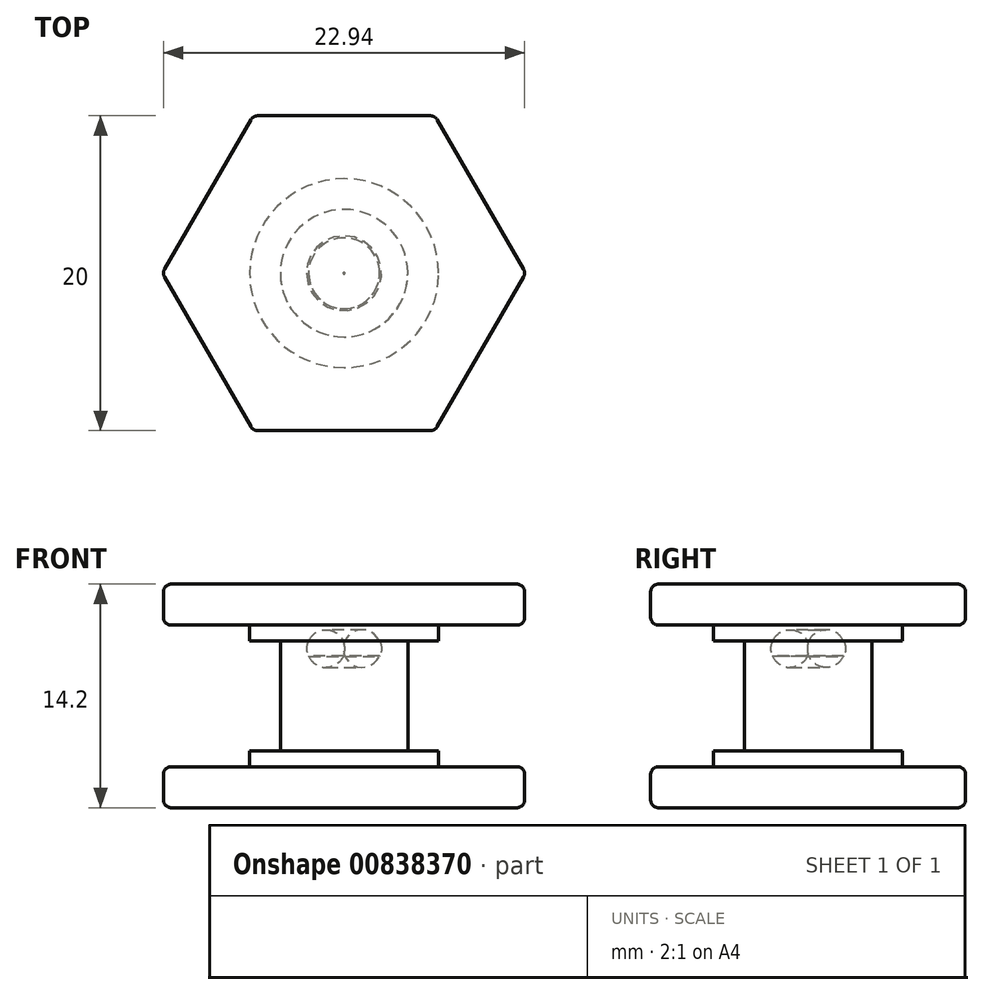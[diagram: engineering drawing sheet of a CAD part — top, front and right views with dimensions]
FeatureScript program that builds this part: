
annotation { "Feature Type Name" : "Feature", "Feature Type Description" : "" }
export const myFeature = defineFeature(function(context is Context, id is Id, definition is map)
    precondition{}
    {
        {
            var Q0;
            Q0=qCreatedBy(makeId("Top.planeOp"),FACE);
            var sketch = newSketch(context, id + "F0", { "sketchPlane" : qUnion([Q0])});
            skCircle(sketch, "E0", {"center": v(0, 0) * mm, "radius": 4.05 * mm});
            skCircle(sketch, "E1", {"center": v(0, 0) * mm, "radius": 6 * mm});
            skSolve(sketch);
        }
        {
            var Q0;
            Q0 = qSketchRegion(id + "F0", true);
            var Q1;
            Q1=makeQuery(id+"F0.imprint","IMPRINT",FACE,{"disambiguationData":[TD([[makeQuery(id+"F0.imprint","IMPRINT",EDGE,{"derivedFrom":sQuery(id+"F0.wireOp",EDGE,"E0")}),1.0]])]});
            extrude(context, id + "F1", {"entities" : qUnion([Q0, Q1]), "depth" : 1 * mm, "offsetDistance" : 25 * mm});
        }
        {
            var Q0;
            Q0=makeQuery(id+"F0.imprint","IMPRINT",FACE,{"disambiguationData":[TD([[makeQuery(id+"F0.imprint","IMPRINT",EDGE,{"derivedFrom":sQuery(id+"F0.wireOp",EDGE,"E0")}),1.0]])]});
            extrude(context, id + "F2", {"entities" : qUnion([Q0]), "operationType" : NewBodyOperationType.ADD, "oppositeDirection" : true, "depth" : 7 * mm, "offsetDistance" : 25 * mm});
        }
        {
            var Q0;
            Q0=makeQuery(id+"F1.opExtrude","CAP_FACE",FACE,{"disambiguationData":[OSD([sQuery(id+"F0.wireOp",EDGE,"E1")])],"isStart":false});
            var sketch = newSketch(context, id + "F3", { "sketchPlane" : qUnion([Q0])});
            skCircle(sketch, "E2.cCircle", {"center": v(0, 0) * mm, "radius": 10 * mm, "construction": true});
            skLineSegment(sketch, "E2.0", {"start": v(5.77, -10) * mm, "end": v(-5.77, -10) * mm});
            skLineSegment(sketch, "E2.1", {"start": v(-5.77, -10) * mm, "end": v(-11.55, 0) * mm});
            skLineSegment(sketch, "E2.2", {"start": v(-11.55, 0) * mm, "end": v(-5.77, 10) * mm});
            skLineSegment(sketch, "E2.3", {"start": v(-5.77, 10) * mm, "end": v(5.77, 10) * mm});
            skLineSegment(sketch, "E2.4", {"start": v(5.77, 10) * mm, "end": v(11.55, 0) * mm});
            skLineSegment(sketch, "E2.5", {"start": v(11.55, 0) * mm, "end": v(5.77, -10) * mm});
            skPoint(sketch, "E2.0.midPoint", {"position": v(0, -10) * mm});
            skSolve(sketch);
        }
        {
            var Q0;
            Q0 = qSketchRegion(id + "F3", true);
            extrude(context, id + "F4", {"entities" : qUnion([Q0]), "operationType" : NewBodyOperationType.ADD, "depth" : 2.6 * mm, "offsetDistance" : 25 * mm});
        }
        {
            var Q0;
            Q0=makeQuery(id+"F2.opExtrude","CAP_FACE",FACE,{"disambiguationData":[OSD([sQuery(id+"F0.wireOp",EDGE,"E0")])],"isStart":false});
            var sketch = newSketch(context, id + "F5", { "sketchPlane" : qUnion([Q0])});
            skCircle(sketch, "E3.0", {"center": v(0, 0) * mm, "radius": 6 * mm});
            skSolve(sketch);
        }
        {
            var Q0;
            Q0=makeQuery(id+"F5.imprint","IMPRINT",FACE,{"disambiguationData":[TD([[makeQuery(id+"F5.imprint","IMPRINT",EDGE,{"derivedFrom":sQuery(id+"F5.wireOp",EDGE,"E3.0")}),1.0]])]});
            var Q1;
            Q1=makeQuery(id+"F5.imprint","IMPRINT",FACE,{"disambiguationData":[TD([[makeQuery(id+"F5.imprint","IMPRINT",EDGE,{"derivedFrom":makeQuery(id+"F2.opExtrude","CAP_EDGE",EDGE,{"disambiguationData":[OSD([sQuery(id+"F0.wireOp",EDGE,"E0")])],"isStart":false})}),-1.0]])]});
            extrude(context, id + "F6", {"entities" : qUnion([Q0, Q1]), "depth" : 1 * mm, "offsetDistance" : 25 * mm});
        }
        {
            var Q0;
            Q0=makeQuery(id+"F6.opExtrude","CAP_FACE",FACE,{"disambiguationData":[OSD([sQuery(id+"F5.wireOp",EDGE,"E3.0")])],"isStart":false});
            var sketch = newSketch(context, id + "F7", { "sketchPlane" : qUnion([Q0])});
            skLineSegment(sketch, "E4.0", {"start": v(11.55, 0) * mm, "end": v(5.77, 10) * mm});
            skLineSegment(sketch, "E4.1", {"start": v(5.77, 10) * mm, "end": v(-5.77, 10) * mm});
            skLineSegment(sketch, "E4.2", {"start": v(-5.77, 10) * mm, "end": v(-11.55, 0) * mm});
            skLineSegment(sketch, "E4.3", {"start": v(-11.55, 0) * mm, "end": v(-5.77, -10) * mm});
            skLineSegment(sketch, "E4.4", {"start": v(-5.77, -10) * mm, "end": v(5.77, -10) * mm});
            skLineSegment(sketch, "E4.5", {"start": v(5.77, -10) * mm, "end": v(11.55, 0) * mm});
            skSolve(sketch);
        }
        {
            var Q0;
            Q0 = qSketchRegion(id + "F7", true);
            extrude(context, id + "F8", {"entities" : qUnion([Q0]), "operationType" : NewBodyOperationType.ADD, "depth" : 2.6 * mm, "offsetDistance" : 25 * mm});
        }
        {
            var Q0;
            Q0=makeQuery(id+"F4.opExtrude","SWEPT_FACE",FACE,{"disambiguationData":[OSD([sQuery(id+"F3.wireOp",EDGE,"E2.5")])]});
            var Q1;
            Q1=makeQuery(id+"F4.opExtrude","SWEPT_FACE",FACE,{"disambiguationData":[OSD([sQuery(id+"F3.wireOp",EDGE,"E2.4")])]});
            var Q2;
            Q2=makeQuery(id+"F4.opExtrude","SWEPT_FACE",FACE,{"disambiguationData":[OSD([sQuery(id+"F3.wireOp",EDGE,"E2.0")])]});
            var Q3;
            Q3=makeQuery(id+"F4.opExtrude","SWEPT_FACE",FACE,{"disambiguationData":[OSD([sQuery(id+"F3.wireOp",EDGE,"E2.1")])]});
            var Q4;
            Q4=makeQuery(id+"F4.opExtrude","SWEPT_FACE",FACE,{"disambiguationData":[OSD([sQuery(id+"F3.wireOp",EDGE,"E2.2")])]});
            var Q5;
            Q5=makeQuery(id+"F4.opExtrude","SWEPT_FACE",FACE,{"disambiguationData":[OSD([sQuery(id+"F3.wireOp",EDGE,"E2.3")])]});
            var Q6;
            Q6=makeQuery(id+"F8.opExtrude","SWEPT_FACE",FACE,{"disambiguationData":[OSD([sQuery(id+"F7.wireOp",EDGE,"E4.1")])]});
            var Q7;
            Q7=makeQuery(id+"F8.opExtrude","SWEPT_FACE",FACE,{"disambiguationData":[OSD([sQuery(id+"F7.wireOp",EDGE,"E4.0")])]});
            var Q8;
            Q8=makeQuery(id+"F8.opExtrude","SWEPT_FACE",FACE,{"disambiguationData":[OSD([sQuery(id+"F7.wireOp",EDGE,"E4.5")])]});
            var Q9;
            Q9=makeQuery(id+"F8.opExtrude","SWEPT_FACE",FACE,{"disambiguationData":[OSD([sQuery(id+"F7.wireOp",EDGE,"E4.4")])]});
            var Q10;
            Q10=makeQuery(id+"F8.opExtrude","SWEPT_FACE",FACE,{"disambiguationData":[OSD([sQuery(id+"F7.wireOp",EDGE,"E4.3")])]});
            var Q11;
            Q11=makeQuery(id+"F8.opExtrude","SWEPT_FACE",FACE,{"disambiguationData":[OSD([sQuery(id+"F7.wireOp",EDGE,"E4.2")])]});
            fillet(context, id + "F9", {"entities" : qUnion([Q0, Q1, Q2, Q3, Q4, Q5, Q6, Q7, Q8, Q9, Q10, Q11]), "radius" : .5 * mm, "tangentPropagation" : true, "allowEdgeOverflow" : false});
        }
        {
            var Q0;
            Q0=makeQuery(id+"F2.opExtrude","CAP_FACE",FACE,{"disambiguationData":[OSD([sQuery(id+"F0.wireOp",EDGE,"E0")])],"isStart":false});
            var sketch = newSketch(context, id + "F10", { "sketchPlane" : qUnion([Q0])});
            skCircle(sketch, "E5", {"center": v(0, 0) * mm, "radius": 2.25 * mm});
            skSolve(sketch);
        }
        {
            var Q0;
            Q0=makeQuery(id+"F10.imprint","IMPRINT",FACE,{"disambiguationData":[TD([[makeQuery(id+"F10.imprint","IMPRINT",EDGE,{"derivedFrom":sQuery(id+"F10.wireOp",EDGE,"E5")}),1.0]])]});
            extrude(context, id + "F11", {"entities" : qUnion([Q0]), "operationType" : NewBodyOperationType.REMOVE, "oppositeDirection" : true, "depth" : 7 * mm, "offsetDistance" : 25 * mm});
        }
        {
            var Q0;
            Q0=qCreatedBy(makeId("Right.planeOp"),FACE);
            var sketch = newSketch(context, id + "F12", { "sketchPlane" : qUnion([Q0])});
            skArc(sketch, "E6", {"start": v(2.25, -1) * mm, "mid": v(2.38, -0.5) * mm, "end": v(2.25, 0) * mm});
            skLineSegment(sketch, "E7", {"start": v(0, 0) * mm, "end": v(0, -7.74) * mm, "construction": true});
            skLineSegment(sketch, "E8", {"start": v(2.25, 0) * mm, "end": v(2.25, -1) * mm});
            skSolve(sketch);
        }
        {
            var Q0;
            Q0 = qSketchRegion(id + "F12", true);
            var Q1;
            Q1=sQuery(id+"F12.wireOp",EDGE,"E7");
            revolve(context, id + "F13", {"operationType" : NewBodyOperationType.REMOVE, "surfaceOperationType" : NewSurfaceOperationType.NEW, "entities" : qUnion([Q0]), "axis" : qUnion([Q1]), "revolveType" : RevolveType.FULL, "oppositeDirection" : true});
        }
        {
            var Q0;
            Q0=makeQuery(id+"F6.opExtrude","CAP_FACE",FACE,{"disambiguationData":[OSD([sQuery(id+"F5.wireOp",EDGE,"E3.0")])],"isStart":true});
            var sketch = newSketch(context, id + "F14", { "sketchPlane" : qUnion([Q0])});
            skCircle(sketch, "E9.0", {"center": v(0, 0) * mm, "radius": 2.25 * mm});
            skSolve(sketch);
        }
        {
            var Q0;
            Q0 = qSketchRegion(id + "F14", true);
            var Q1;
            Q1=makeQuery(id+"F11.boolean.opBoolean","COPY",FACE,{"derivedFrom":makeQuery(id+"F11.opExtrude","CAP_FACE",FACE,{"disambiguationData":[OSD([sQuery(id+"F10.wireOp",EDGE,"E5")])],"isStart":false})});
            extrude(context, id + "F15", {"entities" : qUnion([Q0]), "operationType" : NewBodyOperationType.ADD, "endBound" : BoundingType.UP_TO_SURFACE, "depth" : 25 * mm, "endBoundEntityFace" : qUnion([Q1]), "offsetDistance" : 25 * mm});
        }
        {
            var Q0;
            Q0=qCreatedBy(makeId("Right.planeOp"),FACE);
            var sketch = newSketch(context, id + "F16", { "sketchPlane" : qUnion([Q0])});
            skLineSegment(sketch, "E10", {"start": v(-2.24, 0) * mm, "end": v(-2.24, -0.98) * mm});
            skArc(sketch, "E11", {"start": v(-2.24, 0) * mm, "mid": v(-2.35, -0.5) * mm, "end": v(-2.24, -0.98) * mm});
            skLineSegment(sketch, "E12", {"start": v(0, 0) * mm, "end": v(0, -7.4) * mm, "construction": true});
            skSolve(sketch);
        }
        {
            var Q0;
            Q0 = qSketchRegion(id + "F16", true);
            var Q1;
            Q1=sQuery(id+"F16.wireOp",EDGE,"E12");
            revolve(context, id + "F17", {"operationType" : NewBodyOperationType.ADD, "surfaceOperationType" : NewSurfaceOperationType.NEW, "entities" : qUnion([Q0]), "axis" : qUnion([Q1]), "revolveType" : RevolveType.FULL});
        }
    });
